# Revit family: LCAT-G
name_source: partatom
category: Lighting Fixtures
revit_build: Autodesk Revit 2014 (Build: 20130308_1515(x64)
units: mm (PartAtom-declared; Revit-internal decimal feet)

## types (3) — shared parameters
Apparent Load = 0 VA
Backbox = Hubbell - White
Default Elevation = 48"
Description = LCAT provides both design and value with an architectural appearance, LED technology to reduce maintenance and a wide range of options for classrooms, offices, retail and health care applications
Lamp = LED lamp
Light Bulb = Hubbell - White Glass
Manufacturer = Columbia Lighting
Model = LCAT-G
Voltage = 120 V
Warranty = Five-year warranty
Wattage Comments = 40-80 W

## per-type parameters (varying)
| type | Load Classification | Photometric Web | Product Documentation Link | Product Page URL | Row Length | URL | Width | zz Length |
| LCAT-G-14 | Lighting | Web LCAT : LCAT14-30MLG-EDU | https://hubbellcdn.com | https://www.hubbell.com | 48" | https://www.hubbell.com | 12" | 47" |
| LCAT-G-22 | Other | Web LCAT : LCAT22-40VLG-EDU | http://cdn.columbialighting.com | http://www.columbialighting.com | 24" | http://www.columbialighting.com | 24" | 23" |
| LCAT-G-24 | Other | Web LCAT : LCAT24-40XLG-EDU | http://cdn.columbialighting.com | http://www.columbialighting.com | 48" | http://www.columbialighting.com | 25" | 47" |

## geometry (parser evidence)
native form markers: Sweep x4
no freeform markers — native parametric forms only
